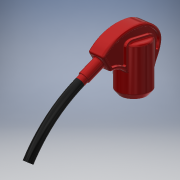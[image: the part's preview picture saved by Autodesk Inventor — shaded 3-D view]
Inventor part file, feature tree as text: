
AUTODESK INVENTOR PART (.ipt)
format: ipt  version: 2018 (Build 220112000, 112)  size: 891,904 bytes
history: native  units: mm
features: fillet x9, sketch x7, extrude x5, projected_geometry x2, revolve x1, plane x1, sweep x1
ambient origin geometry x8: Origin, YZ Plane, XZ Plane, XY Plane, X Axis, Y Axis, Z Axis, Center Point
bodies: Solid1 (feature_tree), Solid2 (feature_tree)
feature tree (26):
  revolve  "Revolution1"  [1 undecoded]
  extrude  "Extrusion1"  Depth=11.2mm
  fillet  "Fillet1"  Radius=1.69mm
  extrude  "Extrusion2"  Depth=5.69mm
  extrude  "Extrusion3"  Depth=1.5mm
  fillet  "Fillet2"  Radius=0.8mm
  fillet  "Fillet3"  Radius=0.25mm
  plane  "Work Plane1"
  sweep  "Sweep1"
  fillet  "Fillet4"  [1 undecoded]
  fillet  "Fillet5"  Radius=2.6mm
  sketch  "Sketch7"  dims[d21=8.5mm d22=4.0mm d23=0.8mm d24=6.0mm d25=0.0mm d26=3.6mm d27=3.0mm d28=6.0mm d29=0.0mm d30=0.5mm d31=0.25mm d32=0.0mm d33=0.0mm d34=0.8mm d35=0.8mm d36=0.2mm d37=0.4mm d38=1.0mm d39=0.0mm d40=0.2mm d41=0.1mm d42=1.0mm d43=0.0mm d44=0.1mm d45=0.2mm]
  extrude  "Extrusion4"  Depth=0.5mm
  fillet  "Fillet6"  Radius=20.0mm
  fillet  "Fillet7"  Radius=5.35mm
  extrude  "Extrusion5"  Depth=0.2mm
  fillet  "Fillet8"  Radius=0.8mm
  fillet  "Fillet9"  Radius=6.0mm
  sketch  "Sketch1"  dims[d0=2.87mm d1=3.87mm d2=5.29mm]
  sketch  "Sketch2"  dims[d3=15.4mm d4=11.2mm d5=1.69mm]
  sketch  "Sketch3"  dims[d6=3.7mm d7=5.69mm]
  sketch  "Sketch4"  dims[d8=2.85mm d9=1.5mm d10=0.8mm d11=0.25mm]
  sketch  "Sketch5"  dims[d12=0.5mm d13=0.25mm d14=90.0deg d15=2.6mm]
  sketch  "Sketch6"  dims[d16=1.22mm d17=0.0mm d18=0.5mm d19=20.0mm d20=5.35mm]
  projected_geometry  "Projected Loop1"
  projected_geometry  "Projected Loop2"
note: 2 required parameter values undecoded (feature->parameter linkage not recoverable at this tier; creation-order binding heuristic only, values carry confidence <= 0.55)